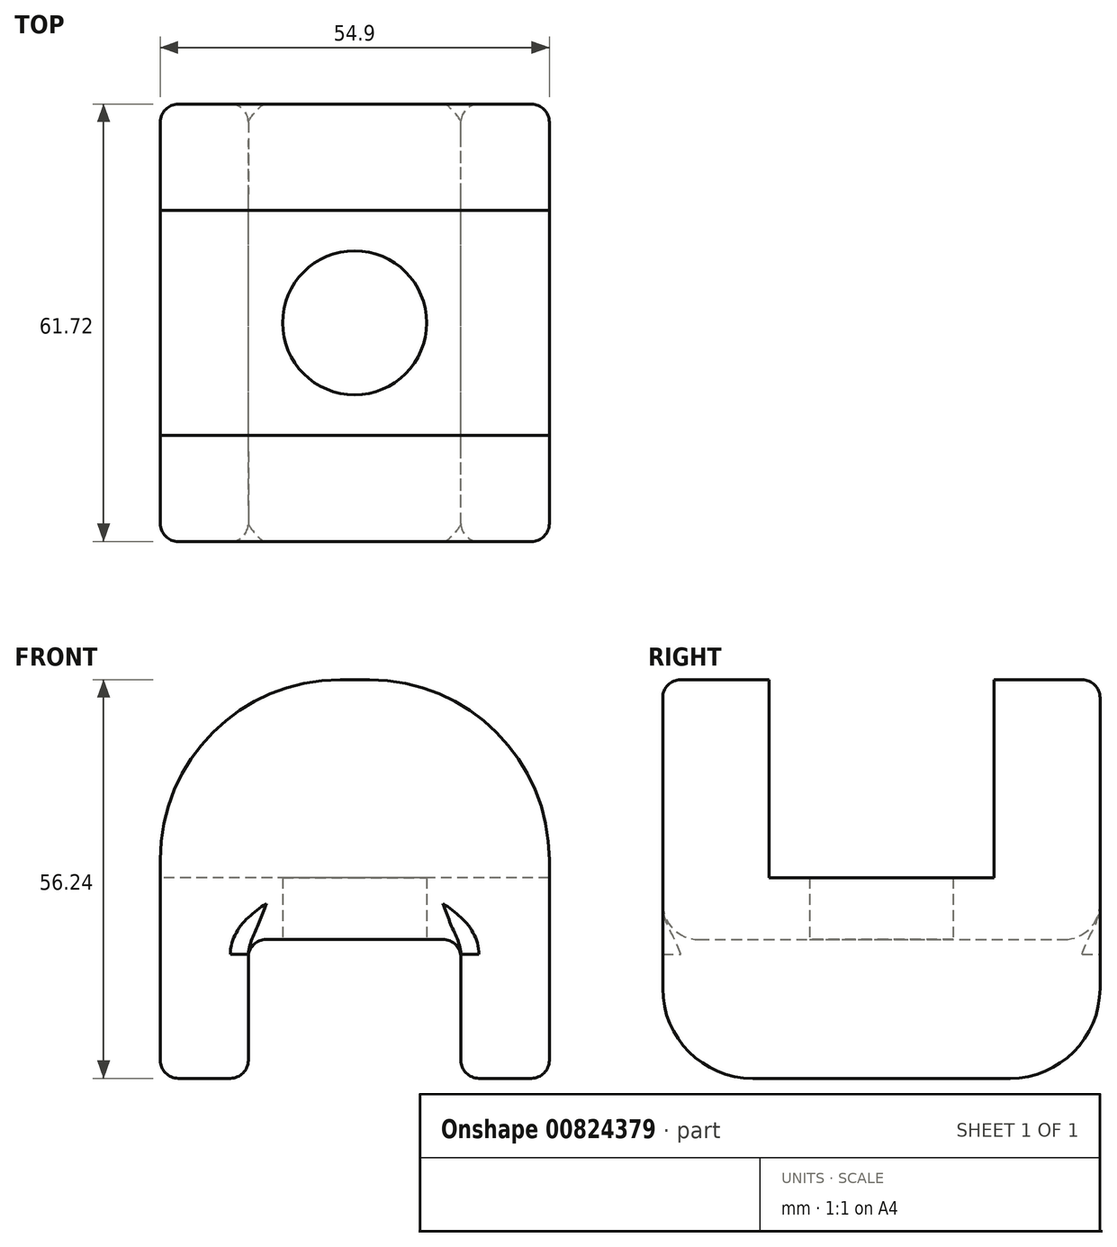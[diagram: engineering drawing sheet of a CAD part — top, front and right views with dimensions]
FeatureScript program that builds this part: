
annotation { "Feature Type Name" : "Feature", "Feature Type Description" : "" }
export const myFeature = defineFeature(function(context is Context, id is Id, definition is map)
    precondition{}
    {
        {
            var Q0;
            Q0=qCreatedBy(makeId("Front.planeOp"),FACE);
            var sketch = newSketch(context, id + "F0", { "sketchPlane" : qUnion([Q0])});
            skLineSegment(sketch, "E0.bottom", {"start": v(0, 0) * mm, "end": v(12.42, 0) * mm});
            skLineSegment(sketch, "E0.top", {"start": v(0, 56.24) * mm, "end": v(54.9, 56.24) * mm});
            skLineSegment(sketch, "E0.left", {"start": v(0, 0) * mm, "end": v(0, 56.24) * mm});
            skLineSegment(sketch, "E0.right", {"start": v(54.9, 0) * mm, "end": v(54.9, 56.24) * mm});
            skLineSegment(sketch, "E1", {"start": v(12.42, 0) * mm, "end": v(12.42, 19.6) * mm});
            skLineSegment(sketch, "E2", {"start": v(12.42, 19.6) * mm, "end": v(42.44, 19.6) * mm});
            skLineSegment(sketch, "E3", {"start": v(42.44, 19.6) * mm, "end": v(42.44, 0) * mm});
            skLineSegment(sketch, "E4.trimOffspring", {"start": v(42.44, 0) * mm, "end": v(54.9, 0) * mm});
            skSolve(sketch);
        }
        {
            var Q0;
            Q0 = qSketchRegion(id + "F0", true);
            extrude(context, id + "F1", {"entities" : qUnion([Q0]), "depth" : 61.72 * mm, "offsetDistance" : 25.4 * mm});
        }
        {
            var Q0;
            Q0=makeQuery(id+"F1.opExtrude","CAP_EDGE",EDGE,{"disambiguationData":[OSD([sQuery(id+"F0.wireOp",EDGE,"E0.bottom")])],"isStart":true});
            var Q1;
            Q1=makeQuery(id+"F1.opExtrude","CAP_EDGE",EDGE,{"disambiguationData":[OSD([sQuery(id+"F0.wireOp",EDGE,"E4.trimOffspring")])],"isStart":true});
            var Q2;
            Q2=makeQuery(id+"F1.opExtrude","CAP_EDGE",EDGE,{"disambiguationData":[OSD([sQuery(id+"F0.wireOp",EDGE,"E4.trimOffspring")])],"isStart":false});
            var Q3;
            Q3=makeQuery(id+"F1.opExtrude","CAP_EDGE",EDGE,{"disambiguationData":[OSD([sQuery(id+"F0.wireOp",EDGE,"E0.bottom")])],"isStart":false});
            fillet(context, id + "F2", {"entities" : qUnion([Q0, Q1, Q2, Q3]), "radius" : 12.7 * mm, "tangentPropagation" : true, "allowEdgeOverflow" : false});
        }
        {
            var Q0;
            Q0=makeQuery(id+"F1.opExtrude","SWEPT_FACE",FACE,{"disambiguationData":[OSD([sQuery(id+"F0.wireOp",EDGE,"E2")])]});
            var sketch = newSketch(context, id + "F3", { "sketchPlane" : qUnion([Q0])});
            skLineSegment(sketch, "E5", {"start": v(27.43, 61.72) * mm, "end": v(27.43, 0) * mm, "construction": true});
            skCircle(sketch, "E6", {"center": v(27.43, 30.86) * mm, "radius": 10.16 * mm});
            skSolve(sketch);
        }
        {
            var Q0;
            Q0 = qSketchRegion(id + "F3", true);
            extrude(context, id + "F4", {"entities" : qUnion([Q0]), "operationType" : NewBodyOperationType.REMOVE, "endBound" : BoundingType.THROUGH_ALL, "oppositeDirection" : true, "depth" : 25.4 * mm, "offsetDistance" : 25.4 * mm});
        }
        {
            var Q0;
            Q0=makeQuery(id+"F1.opExtrude","CAP_EDGE",EDGE,{"disambiguationData":[OSD([sQuery(id+"F0.wireOp",EDGE,"E2")])],"isStart":false});
            var Q1;
            Q1=makeQuery(id+"F1.opExtrude","CAP_EDGE",EDGE,{"disambiguationData":[OSD([sQuery(id+"F0.wireOp",EDGE,"E2")])],"isStart":true});
            fillet(context, id + "F5", {"entities" : qUnion([Q0, Q1]), "radius" : 5.08 * mm, "tangentPropagation" : true, "allowEdgeOverflow" : false});
        }
        {
            var Q0;
            Q0=makeQuery(id+"F1.opExtrude","SWEPT_EDGE",EDGE,{"disambiguationData":[OSD([sQuery(id+"F0.wireOp",EDGE,"E0.top"),sQuery(id+"F0.wireOp",EDGE,"E0.left")])]});
            var Q1;
            Q1=makeQuery(id+"F1.opExtrude","SWEPT_EDGE",EDGE,{"disambiguationData":[OSD([sQuery(id+"F0.wireOp",EDGE,"E0.top"),sQuery(id+"F0.wireOp",EDGE,"E0.right")])]});
            fillet(context, id + "F6", {"entities" : qUnion([Q0, Q1]), "radius" : 25.4 * mm, "tangentPropagation" : true, "allowEdgeOverflow" : false});
        }
        {
            var Q0;
            {var subQ0=sQuery(id+"F0.wireOp",EDGE,"E0.left");var subQ1=sQuery(id+"F0.wireOp",EDGE,"E0.top");Q0=makeQuery(id+"F6.opFillet","BLEND_EDGE",EDGE,{"blendedFrom":[makeQuery(id+"F1.opExtrude","SWEPT_EDGE",EDGE,{"disambiguationData":[OSD([subQ1,subQ0])]}),makeQuery(id+"F1.opExtrude","CAP_FACE",FACE,{"disambiguationData":[OSD([sQuery(id+"F0.wireOp",EDGE,"E0.bottom"),subQ1,subQ0,sQuery(id+"F0.wireOp",EDGE,"E0.right"),sQuery(id+"F0.wireOp",EDGE,"E1"),sQuery(id+"F0.wireOp",EDGE,"E2"),sQuery(id+"F0.wireOp",EDGE,"E3"),sQuery(id+"F0.wireOp",EDGE,"E4.trimOffspring")])],"isStart":true})],"blendedInto":[makeQuery(id+"F1.opExtrude","CAP_FACE",FACE,{"disambiguationData":[OSD([sQuery(id+"F0.wireOp",EDGE,"E0.bottom"),subQ1,subQ0,sQuery(id+"F0.wireOp",EDGE,"E0.right"),sQuery(id+"F0.wireOp",EDGE,"E1"),sQuery(id+"F0.wireOp",EDGE,"E2"),sQuery(id+"F0.wireOp",EDGE,"E3"),sQuery(id+"F0.wireOp",EDGE,"E4.trimOffspring")])],"isStart":true})]});}
            var Q1;
            Q1=makeQuery(id+"F1.opExtrude","CAP_EDGE",EDGE,{"disambiguationData":[OSD([sQuery(id+"F0.wireOp",EDGE,"E1")])],"isStart":true});
            var Q2;
            Q2=makeQuery(id+"F2.opFillet","BLEND_EDGE",EDGE,{"blendedFrom":[makeQuery(id+"F1.opExtrude","CAP_EDGE",EDGE,{"disambiguationData":[OSD([sQuery(id+"F0.wireOp",EDGE,"E4.trimOffspring")])],"isStart":true}),makeQuery(id+"F1.opExtrude","SWEPT_FACE",FACE,{"disambiguationData":[OSD([sQuery(id+"F0.wireOp",EDGE,"E3")])]})],"blendedInto":[makeQuery(id+"F1.opExtrude","SWEPT_FACE",FACE,{"disambiguationData":[OSD([sQuery(id+"F0.wireOp",EDGE,"E3")])]})]});
            var Q3;
            Q3=makeQuery(id+"F5.opFillet","BLEND_EDGE",EDGE,{"blendedFrom":[makeQuery(id+"F1.opExtrude","CAP_EDGE",EDGE,{"disambiguationData":[OSD([sQuery(id+"F0.wireOp",EDGE,"E2")])],"isStart":true}),makeQuery(id+"F1.opExtrude","SWEPT_FACE",FACE,{"disambiguationData":[OSD([sQuery(id+"F0.wireOp",EDGE,"E3")])]})],"blendedInto":[makeQuery(id+"F1.opExtrude","SWEPT_FACE",FACE,{"disambiguationData":[OSD([sQuery(id+"F0.wireOp",EDGE,"E3")])]})]});
            var Q4;
            Q4=makeQuery(id+"F5.opFillet","BLEND_EDGE",EDGE,{"blendedFrom":[makeQuery(id+"F1.opExtrude","CAP_EDGE",EDGE,{"disambiguationData":[OSD([sQuery(id+"F0.wireOp",EDGE,"E2")])],"isStart":true}),makeQuery(id+"F1.opExtrude","SWEPT_FACE",FACE,{"disambiguationData":[OSD([sQuery(id+"F0.wireOp",EDGE,"E1")])]})],"blendedInto":[makeQuery(id+"F1.opExtrude","SWEPT_FACE",FACE,{"disambiguationData":[OSD([sQuery(id+"F0.wireOp",EDGE,"E1")])]})]});
            fillet(context, id + "F7", {"entities" : qUnion([Q0, Q1, Q2, Q3, Q4]), "radius" : 2.54 * mm, "tangentPropagation" : true, "allowEdgeOverflow" : false});
        }
        {
            var Q0;
            Q0=qCreatedBy(makeId("Right.planeOp"),FACE);
            var sketch = newSketch(context, id + "F8", { "sketchPlane" : qUnion([Q0])});
            skLineSegment(sketch, "E7.0", {"start": v(-61.72, 30.84) * mm, "end": v(-61.72, 53.7) * mm, "construction": true});
            skLineSegment(sketch, "E7.1", {"start": v(-61.72, 12.7) * mm, "end": v(-61.72, 30.84) * mm, "construction": true});
            skLineSegment(sketch, "E7.2", {"start": v(0, 53.7) * mm, "end": v(0, 30.84) * mm, "construction": true});
            skLineSegment(sketch, "E7.3", {"start": v(0, 30.84) * mm, "end": v(0, 12.7) * mm, "construction": true});
            skLineSegment(sketch, "E8", {"start": v(0, 53.7) * mm, "end": v(-61.72, 53.7) * mm, "construction": true});
            skLineSegment(sketch, "E9", {"start": v(-30.86, 53.7) * mm, "end": v(-30.86, 28.3) * mm, "construction": true});
            skLineSegment(sketch, "E10", {"start": v(-14.99, 53.7) * mm, "end": v(-14.99, 28.3) * mm});
            skLineSegment(sketch, "E11", {"start": v(-14.99, 28.3) * mm, "end": v(-46.74, 28.3) * mm});
            skLineSegment(sketch, "E12", {"start": v(-46.74, 28.3) * mm, "end": v(-46.74, 53.7) * mm});
            skLineSegment(sketch, "E13", {"start": v(-46.74, 53.7) * mm, "end": v(-14.99, 53.7) * mm});
            skLineSegment(sketch, "E14", {"start": v(-14.99, 53.7) * mm, "end": v(-14.99, 66.3) * mm});
            skLineSegment(sketch, "E15", {"start": v(-46.74, 53.7) * mm, "end": v(-46.74, 66.8) * mm});
            skLineSegment(sketch, "E16", {"start": v(-46.74, 66.8) * mm, "end": v(-14.99, 66.3) * mm});
            skSolve(sketch);
        }
        {
            var Q0;
            Q0 = qSketchRegion(id + "F8", true);
            extrude(context, id + "F9", {"entities" : qUnion([Q0]), "operationType" : NewBodyOperationType.REMOVE, "endBound" : BoundingType.THROUGH_ALL, "depth" : 25.4 * mm, "offsetDistance" : 25.4 * mm});
        }
    });
